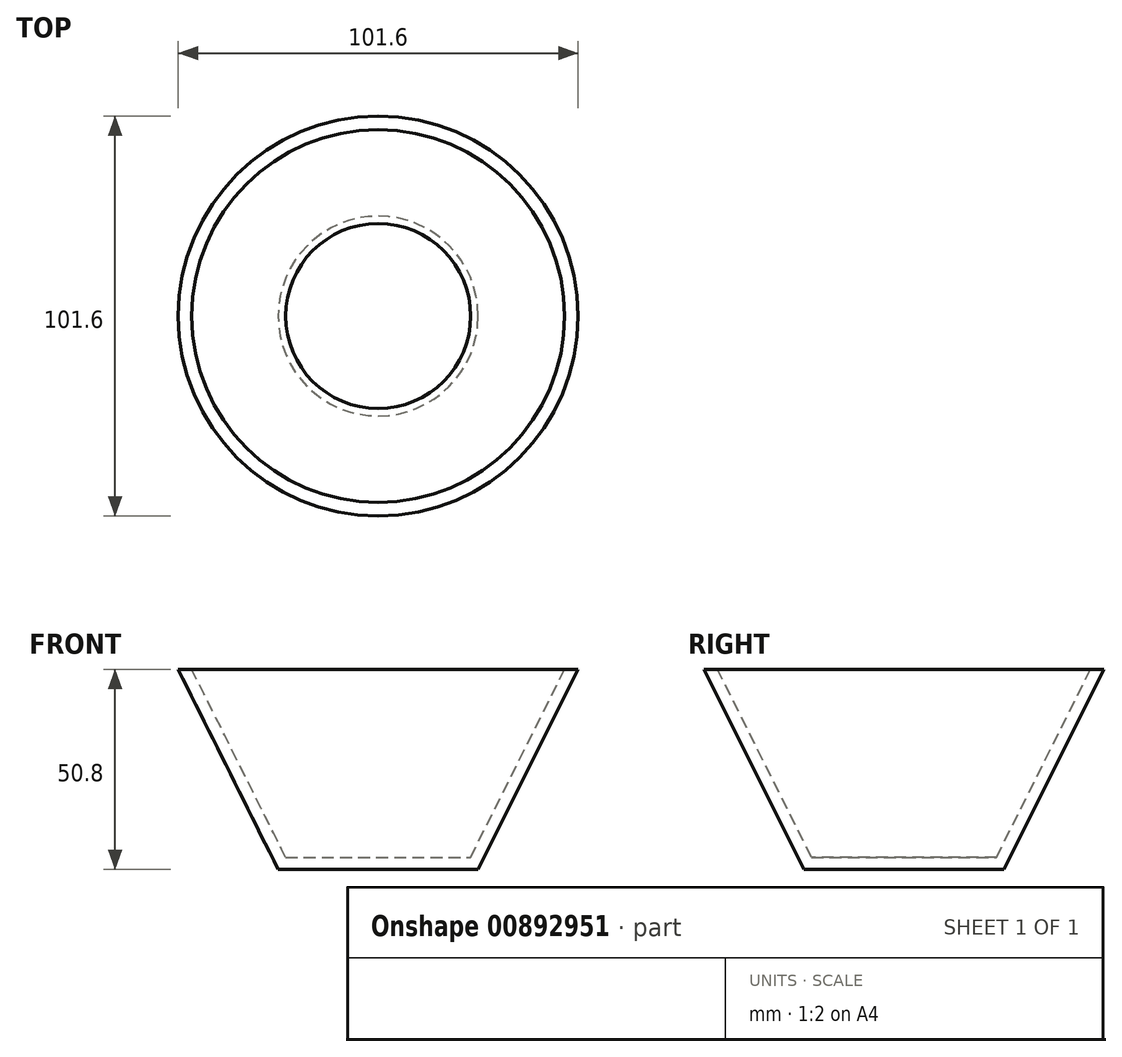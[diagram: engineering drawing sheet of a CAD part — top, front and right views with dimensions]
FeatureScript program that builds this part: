
annotation { "Feature Type Name" : "Feature", "Feature Type Description" : "" }
export const myFeature = defineFeature(function(context is Context, id is Id, definition is map)
    precondition{}
    {
        {
            var Q0;
            Q0=qCreatedBy(makeId("Front.planeOp"),FACE);
            var sketch = newSketch(context, id + "F0", { "sketchPlane" : qUnion([Q0])});
            skLineSegment(sketch, "E0", {"start": v(0, -1.67) * mm, "end": v(0, 49.13) * mm, "construction": true});
            skLineSegment(sketch, "E1", {"start": v(0, -1.67) * mm, "end": v(25.4, -1.67) * mm});
            skLineSegment(sketch, "E2", {"start": v(25.4, -1.67) * mm, "end": v(50.8, 49.13) * mm});
            skLineSegment(sketch, "E3.0", {"start": v(23.5, 1.4) * mm, "end": v(47.36, 49.13) * mm});
            skLineSegment(sketch, "E3.1", {"start": v(0, 1.4) * mm, "end": v(23.5, 1.4) * mm});
            skLineSegment(sketch, "E4", {"start": v(0, -1.67) * mm, "end": v(0, 1.4) * mm});
            skLineSegment(sketch, "E5", {"start": v(47.36, 49.13) * mm, "end": v(50.8, 49.13) * mm});
            skSolve(sketch);
        }
        {
            var Q0;
            Q0=makeQuery(id+"F0.imprint","IMPRINT",FACE,{"disambiguationData":[TD([[makeQuery(id+"F0.imprint","IMPRINT",EDGE,{"derivedFrom":sQuery(id+"F0.wireOp",EDGE,"E1")}),1.0]])]});
            var Q1;
            Q1=sQuery(id+"F0.wireOp",EDGE,"E0");
            revolve(context, id + "F1", {"surfaceOperationType" : NewSurfaceOperationType.NEW, "entities" : qUnion([Q0]), "axis" : qUnion([Q1]), "revolveType" : RevolveType.FULL});
        }
    });
